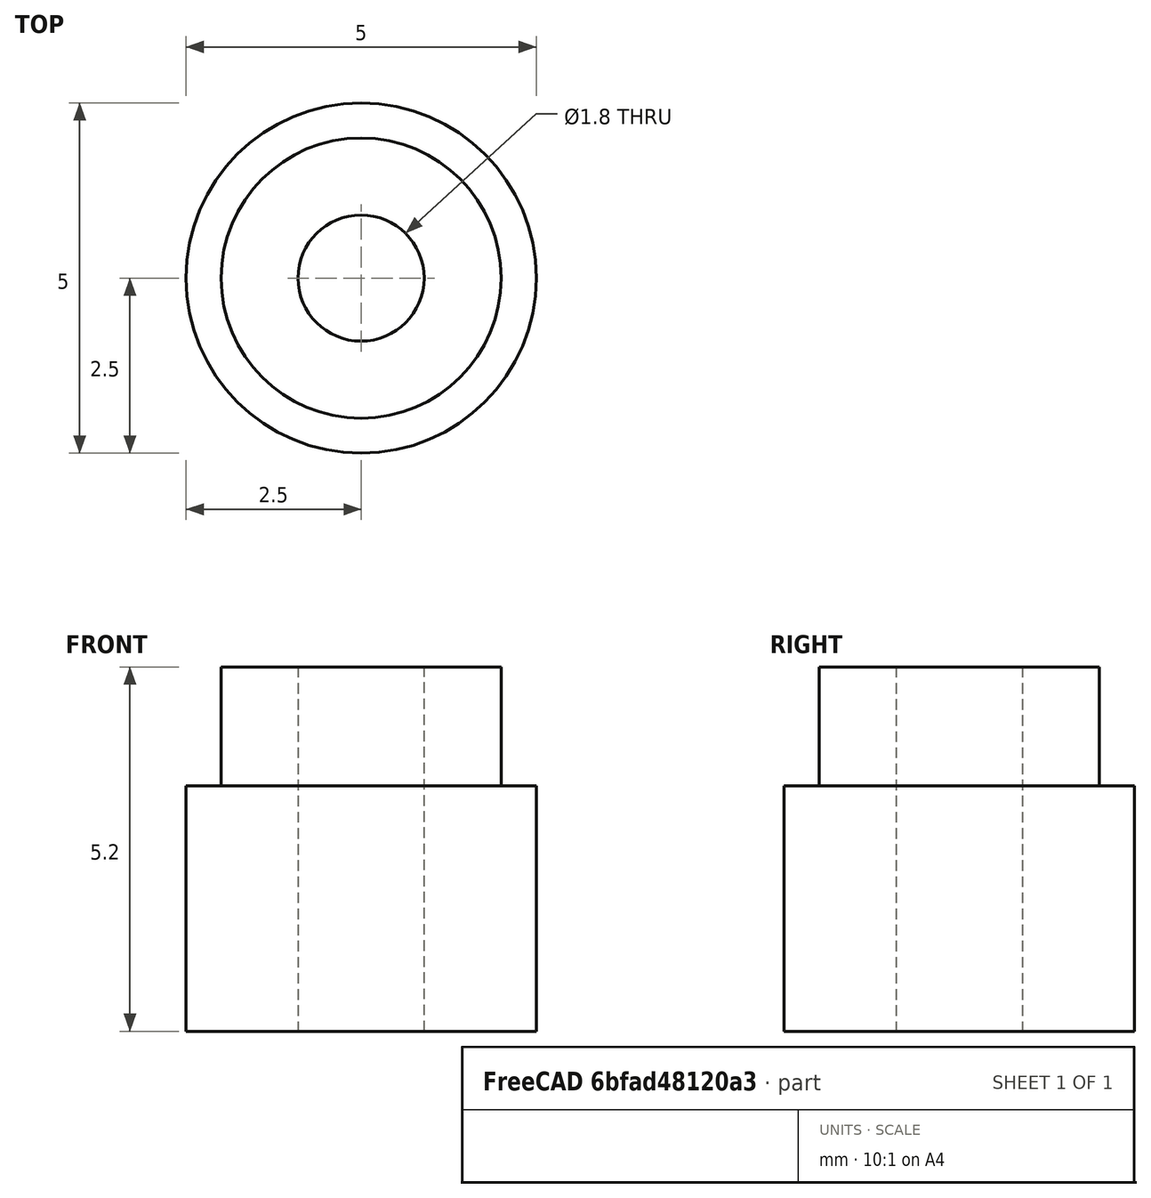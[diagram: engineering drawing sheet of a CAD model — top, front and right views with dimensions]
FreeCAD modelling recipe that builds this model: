
FCSTD DOCUMENT  (FreeCAD 0.22R0.21.2)
Label: 4mmOD_M2_5.5mm
License: All rights reserved
LicenseURL: http://en.wikipedia.org/wiki/All_rights_reserved
objects: Part::Cylinder×3, Part::MultiFuse×1, Part::Cut×1
note: 5 computed .brp shape members not serialized (recipe doc carries the construction recipe); baked Part::Feature solids carry a one-line shape summary decoded from their .brp

FEATURE [Part::Cylinder] Cylinder
  Angle = 360
  AttacherType = Attacher::AttachEngine3D
  FirstAngle = 0
  Height = 3.5
  Radius = 2.5
  SecondAngle = 0
FEATURE [Part::Cylinder] Cylinder001
  Angle = 360
  AttacherType = Attacher::AttachEngine3D
  FirstAngle = 0
  Height = 5.2
  Radius = 2
  SecondAngle = 0
FEATURE [Part::MultiFuse] Fusion
  Shapes = -> [Cylinder001,Cylinder]
FEATURE [Part::Cylinder] Cylinder002
  Angle = 360
  AttacherType = Attacher::AttachEngine3D
  FirstAngle = 0
  Height = 10
  Radius = 0.9
  SecondAngle = 0
FEATURE [Part::Cut] Cut  label="Markor4mmOD_M2"
  Base = -> Fusion
  Tool = -> Cylinder002
